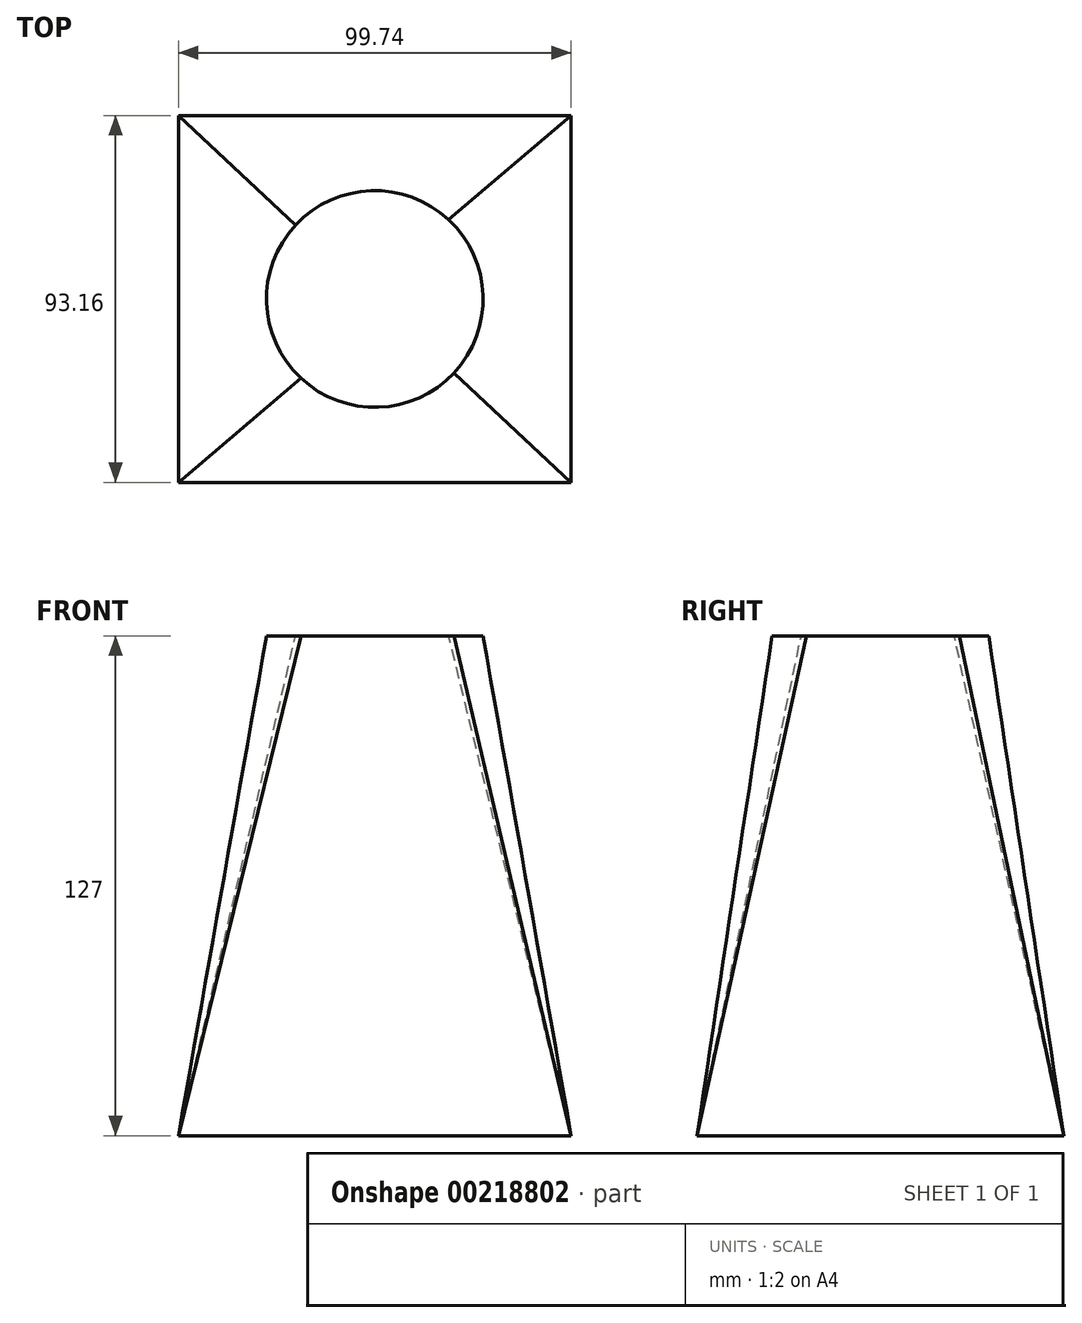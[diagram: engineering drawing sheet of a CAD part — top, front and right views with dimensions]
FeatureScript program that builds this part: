
annotation { "Feature Type Name" : "Feature", "Feature Type Description" : "" }
export const myFeature = defineFeature(function(context is Context, id is Id, definition is map)
    precondition{}
    {
        {
            var Q0;
            Q0=qCreatedBy(makeId("Top.planeOp"),FACE);
            cPlane(context, id + "F0", {"entities" : qUnion([Q0]), "cplaneType" : CPlaneType.OFFSET, "offset" : 127 * mm, "width" : 152.4 * mm, "height" : 152.4 * mm});
        }
        {
            var Q0;
            Q0=qCreatedBy(makeId("Top.planeOp"),FACE);
            var sketch = newSketch(context, id + "F1", { "sketchPlane" : qUnion([Q0])});
            skLineSegment(sketch, "E0.bottom", {"start": v(49.87, -46.58) * mm, "end": v(-49.87, -46.58) * mm});
            skLineSegment(sketch, "E0.top", {"start": v(49.87, 46.58) * mm, "end": v(-49.87, 46.58) * mm});
            skLineSegment(sketch, "E0.left", {"start": v(49.87, -46.58) * mm, "end": v(49.87, 46.58) * mm});
            skLineSegment(sketch, "E0.right", {"start": v(-49.87, -46.58) * mm, "end": v(-49.87, 46.58) * mm});
            skPoint(sketch, "E0.middle", {"position": v(0, 0) * mm});
            skSolve(sketch);
        }
        {
            var Q0;
            Q0=qCreatedBy(id+"F0.planeOp",FACE);
            var sketch = newSketch(context, id + "F2", { "sketchPlane" : qUnion([Q0])});
            skCircle(sketch, "E1", {"center": v(0, 0) * mm, "radius": 27.52 * mm});
            skSolve(sketch);
        }
        {
            var Q0;
            Q0=makeQuery(id+"F1.imprint","IMPRINT",FACE,{"disambiguationData":[TD([[makeQuery(id+"F1.imprint","IMPRINT",EDGE,{"derivedFrom":sQuery(id+"F1.wireOp",EDGE,"E0.bottom")}),-1.0]])]});
            var Q1;
            Q1=makeQuery(id+"F2.imprint","IMPRINT",FACE,{"disambiguationData":[TD([[makeQuery(id+"F2.imprint","IMPRINT",EDGE,{"derivedFrom":sQuery(id+"F2.wireOp",EDGE,"E1")}),1.0]])]});
            loft(context, id + "F3", {"sheetProfilesArray" : [{ "sheetProfileEntities" : qUnion([Q0]) }, { "sheetProfileEntities" : qUnion([Q1]) }]});
        }
    });
